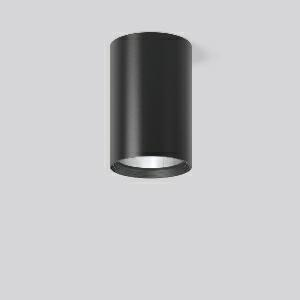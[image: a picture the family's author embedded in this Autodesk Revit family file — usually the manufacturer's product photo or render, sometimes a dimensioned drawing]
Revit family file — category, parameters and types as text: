
# Revit family: heledon_maxi_a_931217_003_3_76_995d
name_source: partatom
category: Lighting Fixtures
units: mm (PartAtom-declared; Revit-internal decimal feet)

## family parameters
Cut with Voids When Loaded = No
Host = Face
Light Source = No
Part Type = Normal
Room Calculation Point = No
Round Connector Dimension = Use Diameter
Shared = No

## types (1)
- HELEDON maxi A (1 x LED Modul 935, 3400 lm, 3500)
    Apparent Load = 25 VA
    Approval mark = CE
    CIE Flux Codes = 100 100 100 100 100
    Color Rendering = 92
    Color Temperature = 3500
    Default Elevation = 1800 mm
    Description = Series: HELEDON maxi
Cylindrical surface-mounted downlight. Housing: die-cast aluminium, powder-coated. Internal ceiling frame polycarbonate with bayonet mounting. Black plastic ring and recessed LED to prevent glare from the side. Optical assembly with reflector made of MIRO-Silver with 98% total light reflection for outstanding efficiency - can be changed without tools. Best colour rendering index Ra>90. Suitable for Ceiling mounting. Easy installation with a separate ceiling frame with bayonet mounting and plug connection. Driver integrated. Connected via plug-in connector. High quality converter without flickering and stroboscopic effect. The following accessories can be mounted without use of tools: interchangeable lenses, decorative glasses, honeycomb louvre, clear and frosted diffusers, white interchangeable plastic ring. 
Colour: deep black, matt (RAL 9005)
Diameter: 123 mm
Height: 183 mm
Lamp: LED
Socket: without socket
Colour temperature: 3500K
Colour rendering index (CRI): 92
System power: 25 W
Rated luminous flux: 3400 lm
Luminous efficiency: 136 lm/W
Control gear: Converter, dimmable, DALI
Protection class: I
Type of protection: IP 20
    Height = 183 mm
    Lamp = 1 x LED Modul 935
    Lamp Light Flux = 3400 lm
    Lamp count = 1
    Length = 123 mm
    Lifetime = 50000 h
    Luminous efficacy = 136 lm/W
    Manufacturer = RZB
    ModVariant = No
    Model = 931217.003.3.76
    Mounting Place = Ceiling
    Mounting Type = Surface mounted
    Number of Poles = 1
    OnlyDefault = Yes
    Power Factor = 1
    Product Name = HELEDON maxi A
    Product group = Surface mounted downlights
    ProductGroupID = 302
    Protection Class = Protection class I
    Protection Degree = IP 20
    RLX_Detail_Level = 1
    RLX_Emergency_Light_Flux = 0 lm
    RLX_Emergency_Type = 0
    RLX_Emergency_Type_DB = No
    RlxData = <blob elided: 98853 chars, md5=35bcfe5f>
    Socket = socket
    Standby Power = 0 W
    System Light Flux = 3400 lm
    System Power = 25 W
    Type Comments = Product without accessories
    Type Image = 931192.003.jpg
    URL = http://relux.com
    VarID = ---
    Voltage = 230 V
    Voltage Range = 220-240 V
    Weight = 0.00 kg
    Width = 0 mm  [stored 0 ft]

note: [stored X ft] marks values corroborated as IEEE doubles in the binary element streams (Revit-internal decimal feet)

## geometry (parser evidence)
native form markers: Blend x4, Sweep x10
no freeform markers — native parametric forms only
